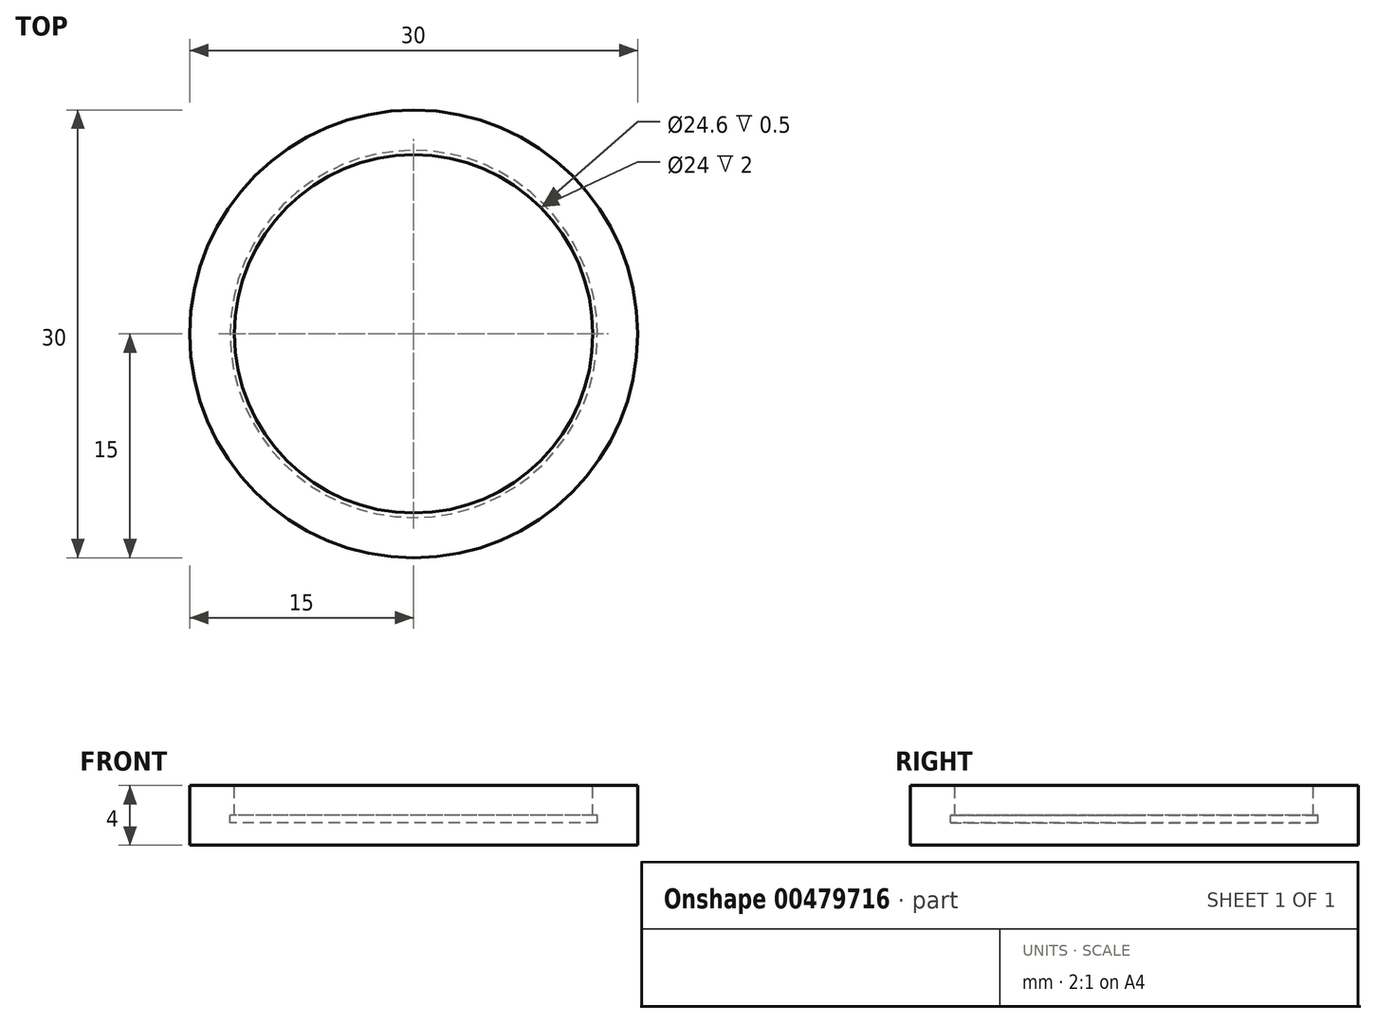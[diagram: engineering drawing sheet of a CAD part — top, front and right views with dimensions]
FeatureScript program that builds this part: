
annotation { "Feature Type Name" : "Feature", "Feature Type Description" : "" }
export const myFeature = defineFeature(function(context is Context, id is Id, definition is map)
    precondition{}
    {
        {
            var Q0;
            Q0=qCreatedBy(makeId("Front.planeOp"),FACE);
            var sketch = newSketch(context, id + "F0", { "sketchPlane" : qUnion([Q0])});
            skLineSegment(sketch, "E0", {"start": v(0, 0) * mm, "end": v(-15, 0) * mm});
            skLineSegment(sketch, "E1", {"start": v(-15, 0) * mm, "end": v(-15, 4) * mm});
            skLineSegment(sketch, "E2", {"start": v(-15, 4) * mm, "end": v(-12, 4) * mm});
            skLineSegment(sketch, "E3", {"start": v(-12, 4) * mm, "end": v(-12, 2) * mm});
            skLineSegment(sketch, "E4", {"start": v(-12, 2) * mm, "end": v(-12.3, 2) * mm});
            skLineSegment(sketch, "E5", {"start": v(-12.3, 2) * mm, "end": v(-12.3, 1.5) * mm});
            skLineSegment(sketch, "E6", {"start": v(-12.3, 1.5) * mm, "end": v(0, 1.5) * mm});
            skLineSegment(sketch, "E7", {"start": v(0, 1.5) * mm, "end": v(0, 0) * mm});
            skSolve(sketch);
        }
        {
            var Q0;
            Q0=makeQuery(id+"F0.imprint","IMPRINT",FACE,{"disambiguationData":[TD([[makeQuery(id+"F0.imprint","IMPRINT",EDGE,{"derivedFrom":sQuery(id+"F0.wireOp",EDGE,"E0")}),-1.0]])]});
            var Q1;
            Q1=sQuery(id+"F0.wireOp",EDGE,"E7");
            revolve(context, id + "F1", {"entities" : qUnion([Q0]), "axis" : qUnion([Q1]), "revolveType" : RevolveType.FULL});
        }
    });
